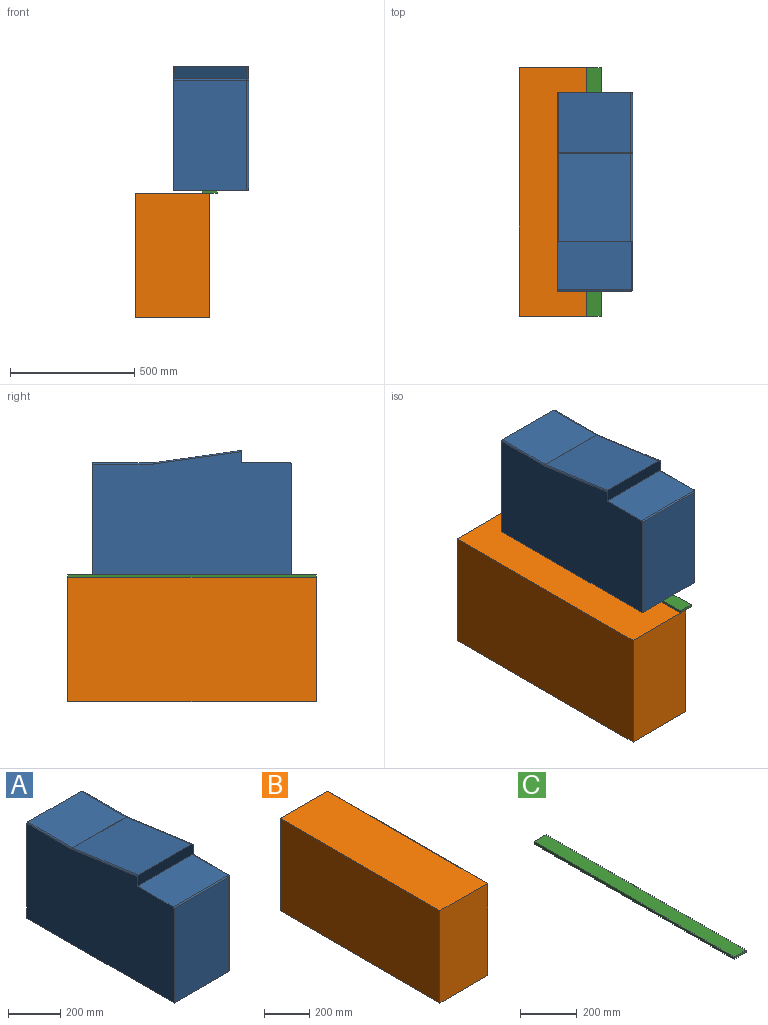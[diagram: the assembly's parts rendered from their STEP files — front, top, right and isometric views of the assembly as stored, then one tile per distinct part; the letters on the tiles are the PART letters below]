
ASSEMBLY  parts=3 mates=2
PART A: 21 faces, bbox 305.8x800.8x500 mm
  f0: plane 355.42x290mm, normal (0,0.14,0.99), area 104085.4mm2, adj f15,f17,f18
  f1: plane 780x479.9mm, normal (1,0,0), area 345209.3mm2, adj f9,f11,f12,f13,f14,f15,f16
  f2: plane 800x494.95mm, normal (-1,0,0), area 365871.4mm2, adj f4,f5,f6,f7,f8,f18,f19,f20
  f3: plane 290x243.88mm, normal (0,0,1), area 70725.7mm2, adj f5,f14,f17,f20
  f4: plane 445x295mm, normal (0,-1,0), area 131275mm2, adj f2,f6,f8,f11
  f5: plane 450x295mm, normal (0,1,0), area 132744.6mm2, adj f2,f3,f6,f13,f20
  f6: plane 800x295mm, normal (0,0,-1), area 236000mm2, adj f2,f4,f5,f12
  f7: plane 300x195mm, normal (0,0,1), area 58494.6mm2, adj f2,f8,f9,f10
  f8: cylinder r=5mm len=295mm, axis (-1,0,0), area 2316.9mm2, adj f2,f4,f7,f10
  f9: cylinder r=5mm len=190mm, axis (0,-1,0), area 1492.3mm2, adj f1,f7,f10
  f10: torus R=5mm, axis (0,0,1), area 101mm2, adj f7,f8,f9,f11
  f11: cylinder r=10mm len=445mm, axis (0,0,1), area 6933mm2, adj f1,f4,f10,f12
  f12: cylinder r=10mm len=800mm, axis (0,1,0), area 12452.2mm2, adj f1,f6,f11,f13
  f13: cylinder r=10mm len=450mm, axis (0,0,1), area 6954.4mm2, adj f1,f5,f12,f14
  f14: cylinder r=10mm len=243.88mm, axis (0,1,0), area 3773.8mm2, adj f1,f3,f13,f16
  f15: cylinder r=10mm len=356.81mm, axis (0,-0.99,0.14), area 5629.8mm2, adj f0,f1,f16
  f16: torus R=15mm, axis (1,0,0), area 18.9mm2, adj f1,f14,f15,f17
  f17: cylinder r=5mm len=290mm, axis (1,0,0), area 202.5mm2, adj f0,f3,f16,f19
  f18: cylinder r=5mm len=356.12mm, axis (0,-0.99,0.14), area 2816.9mm2, adj f0,f2,f19
  f19: torus R=10mm, axis (1,0,0), area 7.5mm2, adj f2,f17,f18,f20
  f20: cylinder r=5mm len=243.88mm, axis (0,1,0), area 1915.4mm2, adj f2,f3,f5,f19
PART B: 7 faces, bbox 300x1000x500 mm
  f0: plane 1000x295mm, normal (0,0,1), area 295000mm2, adj f1,f4,f5,f6
  f1: plane 1000x500mm, normal (-1,0,0), area 500000mm2, adj f0,f2,f4,f5
  f2: plane 1000x300mm, normal (0,0,-1), area 300000mm2, adj f1,f3,f4,f5
  f3: plane 1000x495mm, normal (1,0,0), area 495000mm2, adj f2,f4,f5,f6
  f4: plane 500x300mm, normal (0,-1,0), area 149994.6mm2, adj f0,f1,f2,f3,f6
  f5: plane 500x300mm, normal (0,1,0), area 149994.6mm2, adj f0,f1,f2,f3,f6
  f6: cylinder r=5mm len=1000mm, axis (0,1,0), area 7854mm2, adj f0,f3,f4,f5
PART C: 6 faces, bbox 60x1000x10 mm
  f0: plane 1000x60mm, normal (0,0,1), area 60000mm2, adj f1,f3,f4,f5
  f1: plane 1000x10mm, normal (-1,0,0), area 10000mm2, adj f0,f2,f4,f5
  f2: plane 1000x60mm, normal (0,0,-1), area 60000mm2, adj f1,f3,f4,f5
  f3: plane 1000x10mm, normal (1,0,0), area 10000mm2, adj f0,f2,f4,f5
  f4: plane 60x10mm, normal (0,-1,0), area 600mm2, adj f0,f1,f2,f3
  f5: plane 60x10mm, normal (0,1,0), area 600mm2, adj f0,f1,f2,f3
PLACE A t=(0,0,-3.27)mm
PLACE B t=(-152.5,-100,30.12)mm
PLACE C t=(-152.5,-100,200)mm
MATE planar C.f2 <-> B.f0  axis (0,0,-1) through (-2.5,-100,-20.13)mm
MATE planar A.f6 <-> C.f0  axis (0,0,-1) through (-2.5,-100,-10.13)mm
